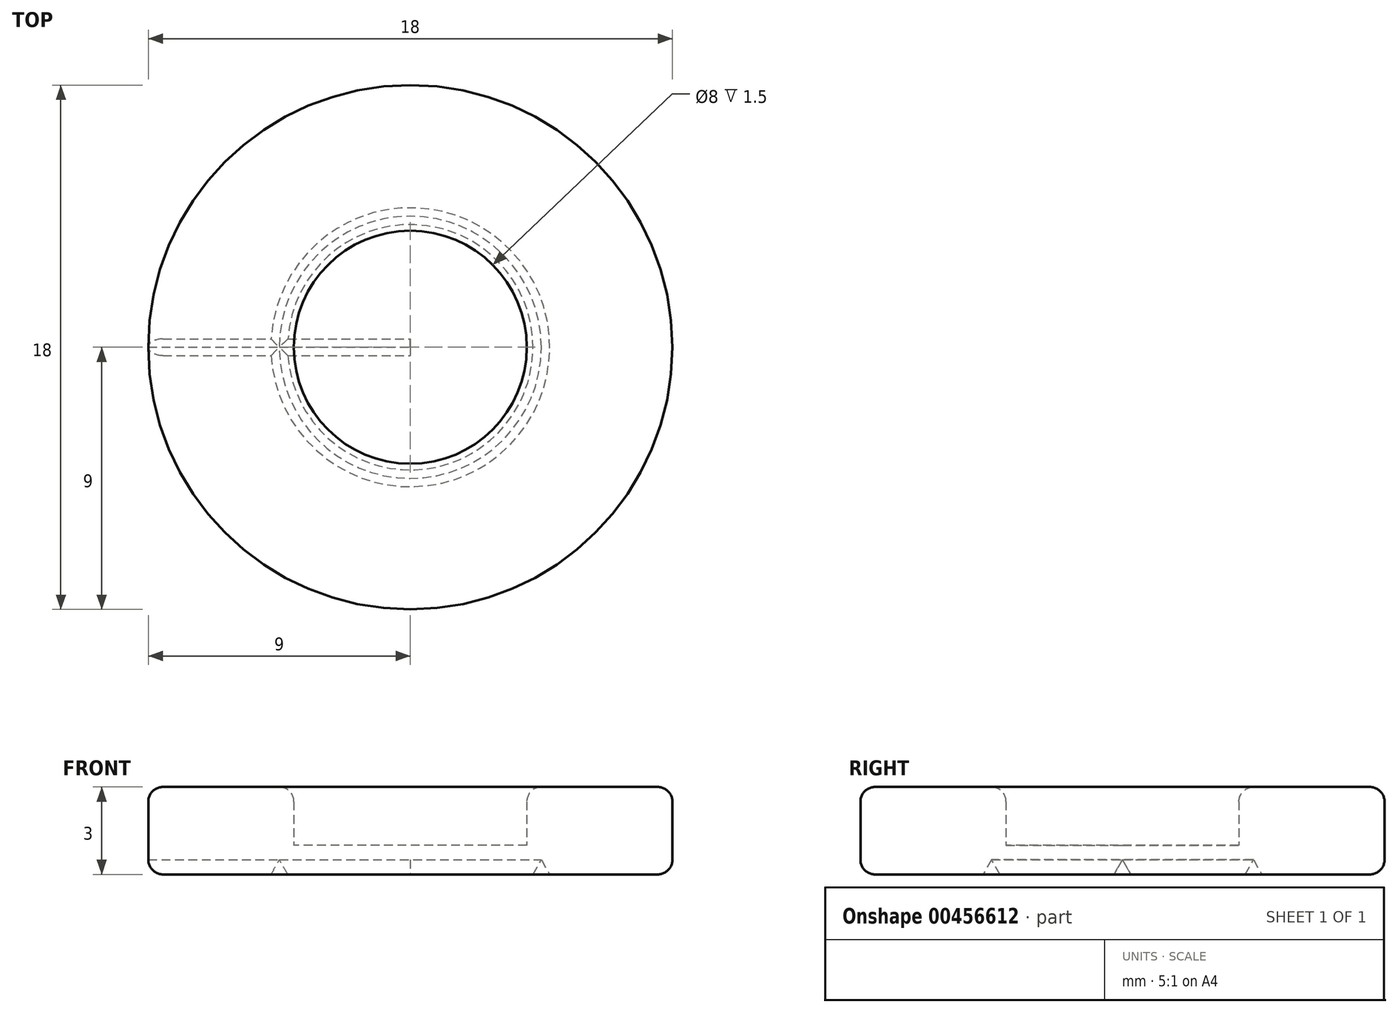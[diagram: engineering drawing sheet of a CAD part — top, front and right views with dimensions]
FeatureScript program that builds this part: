
annotation { "Feature Type Name" : "Feature", "Feature Type Description" : "" }
export const myFeature = defineFeature(function(context is Context, id is Id, definition is map)
    precondition{}
    {
        {
            var Q0;
            Q0=qCreatedBy(makeId("Top.planeOp"),FACE);
            var sketch = newSketch(context, id + "F0", { "sketchPlane" : qUnion([Q0])});
            skCircle(sketch, "E0", {"center": v(0, 0) * mm, "radius": 4 * mm});
            skCircle(sketch, "E1.0", {"center": v(0, 0) * mm, "radius": 9 * mm});
            skSolve(sketch);
        }
        {
            var Q0;
            Q0 = qSketchRegion(id + "F0", true);
            extrude(context, id + "F1", {"entities" : qUnion([Q0]), "depth" : 3 * mm});
        }
        {
            var Q0;
            Q0=makeQuery(id+"F1.opExtrude","CAP_FACE",FACE,{"disambiguationData":[OSD([sQuery(id+"F0.wireOp",EDGE,"E0"),sQuery(id+"F0.wireOp",EDGE,"E1.0")])],"isStart":true});
            var sketch = newSketch(context, id + "F2", { "sketchPlane" : qUnion([Q0])});
            skCircle(sketch, "E2.0", {"center": v(0, 0) * mm, "radius": 4 * mm});
            skSolve(sketch);
        }
        {
            var Q0;
            Q0 = qSketchRegion(id + "F2", true);
            extrude(context, id + "F3", {"entities" : qUnion([Q0]), "operationType" : NewBodyOperationType.ADD, "oppositeDirection" : true, "depth" : 1 * mm});
        }
        {
            var Q0;
            Q0=makeQuery(id+"F1.opExtrude","CAP_EDGE",EDGE,{"disambiguationData":[OSD([sQuery(id+"F0.wireOp",EDGE,"E1.0")])],"isStart":true});
            var Q1;
            Q1=makeQuery(id+"F1.opExtrude","CAP_EDGE",EDGE,{"disambiguationData":[OSD([sQuery(id+"F0.wireOp",EDGE,"E1.0")])],"isStart":false});
            fillet(context, id + "F4", {"entities" : qUnion([Q0, Q1]), "radius" : .5 * mm, "tangentPropagation" : true, "allowEdgeOverflow" : false});
        }
        {
            var Q0;
            Q0=qCreatedBy(makeId("Right.planeOp"),FACE);
            var sketch = newSketch(context, id + "F5", { "sketchPlane" : qUnion([Q0])});
            skLineSegment(sketch, "E3.0", {"start": v(0.29, 0) * mm, "end": v(-0.29, 0) * mm});
            skLineSegment(sketch, "E4", {"start": v(0, 0) * mm, "end": v(0, 0.5) * mm, "construction": true});
            skLineSegment(sketch, "E5", {"start": v(0, 0.5) * mm, "end": v(-0.29, 0) * mm});
            skLineSegment(sketch, "E6", {"start": v(0, 0.5) * mm, "end": v(0.29, 0) * mm});
            skPoint(sketch, "E7.orphan", {"position": v(8.5, 0) * mm});
            skPoint(sketch, "E8.orphan", {"position": v(-8.5, 0) * mm});
            skSolve(sketch);
        }
        {
            var Q0;
            Q0 = qSketchRegion(id + "F5", true);
            extrude(context, id + "F6", {"entities" : qUnion([Q0]), "operationType" : NewBodyOperationType.REMOVE, "endBound" : BoundingType.THROUGH_ALL, "oppositeDirection" : true, "depth" : 25 * mm});
        }
        {
            var Q0;
            Q0=qCreatedBy(makeId("Right.planeOp"),FACE);
            var sketch = newSketch(context, id + "F7", { "sketchPlane" : qUnion([Q0])});
            skLineSegment(sketch, "E9", {"start": v(4.21, 0) * mm, "end": v(4.79, 0) * mm});
            skLineSegment(sketch, "E10", {"start": v(4.5, 0.5) * mm, "end": v(4.79, 0) * mm});
            skLineSegment(sketch, "E11", {"start": v(4.5, 0.5) * mm, "end": v(4.21, 0) * mm});
            skSolve(sketch);
        }
        {
            var Q0;
            Q0=qCreatedBy(makeId("Right.planeOp"),FACE);
            var sketch = newSketch(context, id + "F8", { "sketchPlane" : qUnion([Q0])});
            skLineSegment(sketch, "E12", {"start": v(0, 0) * mm, "end": v(0, 1) * mm, "construction": true});
            skSolve(sketch);
        }
        {
            var Q0;
            Q0 = qSketchRegion(id + "F7", true);
            var Q1;
            Q1 = qConstructionFilter(qBodyType(qCreatedBy(id + "F7" ,EDGE), BodyType.WIRE), ConstructionObject.NO);
            var Q2;
            Q2=sQuery(id+"F8.wireOp",EDGE,"E12");
            revolve(context, id + "F9", {"operationType" : NewBodyOperationType.REMOVE, "entities" : qUnion([Q0]), "surfaceEntities" : qUnion([Q1]), "axis" : qUnion([Q2]), "revolveType" : RevolveType.FULL});
        }
        {
            var Q0;
            Q0=makeQuery(id+"F1.opExtrude","CAP_EDGE",EDGE,{"disambiguationData":[OSD([sQuery(id+"F0.wireOp",EDGE,"E0")])],"isStart":false});
            fillet(context, id + "F10", {"entities" : qUnion([Q0]), "radius" : .5 * mm, "tangentPropagation" : true, "allowEdgeOverflow" : false});
        }
    });
